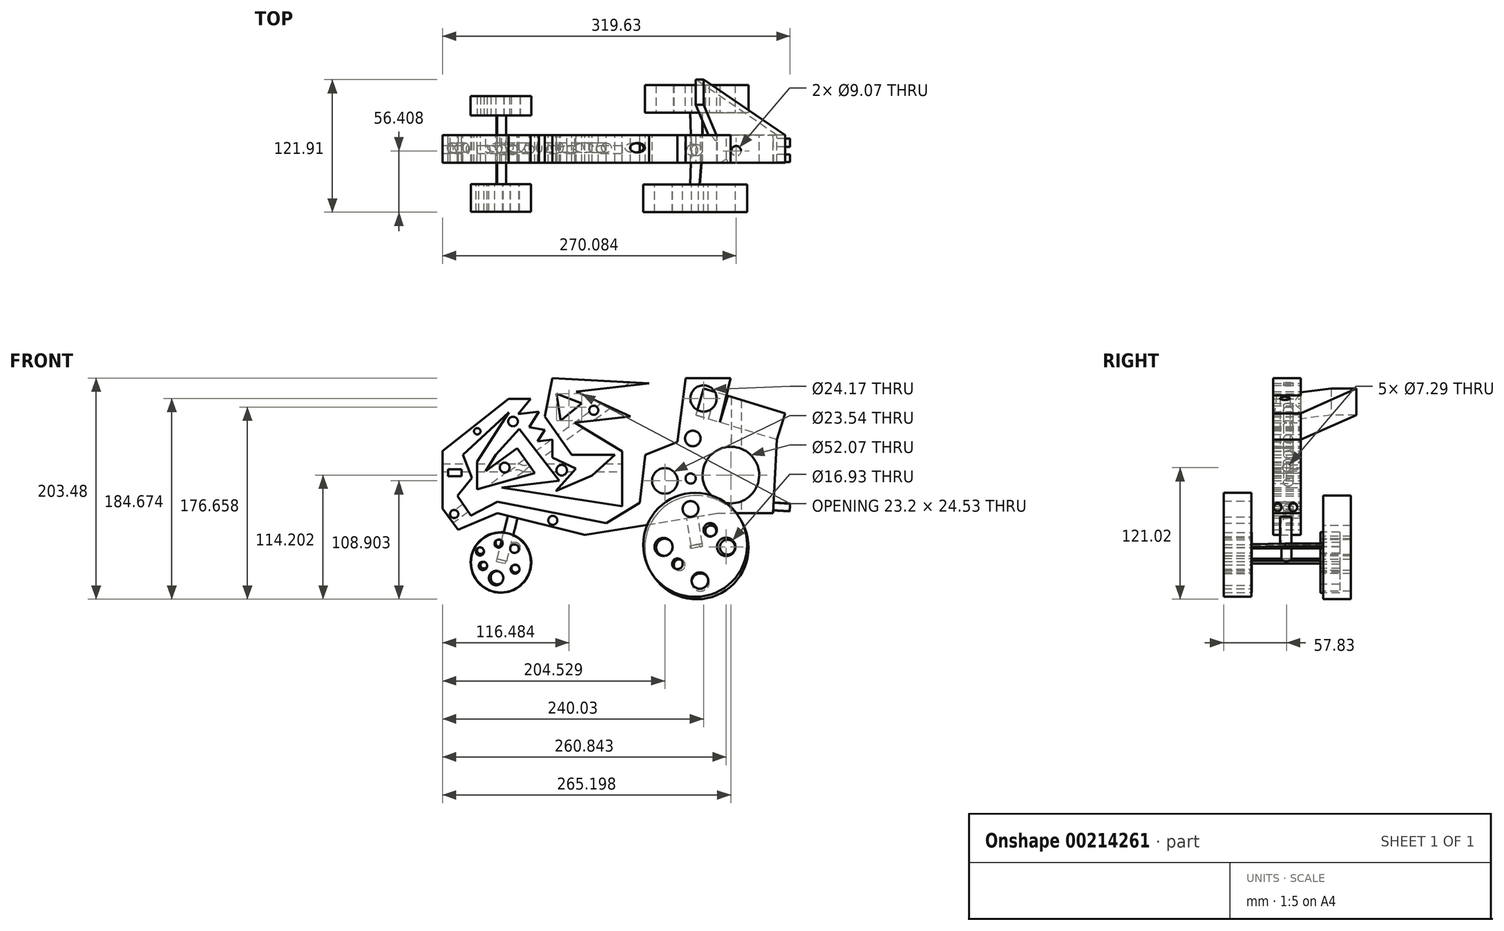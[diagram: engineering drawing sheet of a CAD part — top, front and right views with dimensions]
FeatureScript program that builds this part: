
annotation { "Feature Type Name" : "Feature", "Feature Type Description" : "" }
export const myFeature = defineFeature(function(context is Context, id is Id, definition is map)
    precondition{}
    {
        {
            var Q0;
            Q0=qCreatedBy(makeId("Front.planeOp"),FACE);
            var sketch = newSketch(context, id + "F0", { "sketchPlane" : qUnion([Q0])});
            skLineSegment(sketch, "E0", {"start": v(-109.42, 0) * mm, "end": v(-87.7, 23.84) * mm});
            skLineSegment(sketch, "E1", {"start": v(-87.7, 23.84) * mm, "end": v(-50.87, -23.58) * mm});
            skLineSegment(sketch, "E2", {"start": v(-50.87, -23.58) * mm, "end": v(-104.12, -29.94) * mm});
            skLineSegment(sketch, "E3", {"start": v(-104.12, -29.94) * mm, "end": v(6.89, -47.16) * mm});
            skLineSegment(sketch, "E4", {"start": v(6.89, -47.16) * mm, "end": v(6.89, 3.18) * mm});
            skLineSegment(sketch, "E5", {"start": v(6.89, 3.18) * mm, "end": v(-36.56, 29.67) * mm});
            skLineSegment(sketch, "E6", {"start": v(-36.56, 29.67) * mm, "end": v(14.3, 35.5) * mm});
            skLineSegment(sketch, "E7", {"start": v(14.3, 35.5) * mm, "end": v(-35.5, 58.28) * mm});
            skLineSegment(sketch, "E8", {"start": v(-35.5, 58.28) * mm, "end": v(31.53, 65.7) * mm});
            skLineSegment(sketch, "E9", {"start": v(31.53, 65.7) * mm, "end": v(-57.5, 70.73) * mm});
            skLineSegment(sketch, "E10", {"start": v(-57.5, 70.73) * mm, "end": v(-64.38, 35.5) * mm});
            skLineSegment(sketch, "E11", {"start": v(-64.38, 35.5) * mm, "end": v(-39.48, 0) * mm});
            skLineSegment(sketch, "E12", {"start": v(-39.48, 0) * mm, "end": v(0, 0) * mm});
            skLineSegment(sketch, "E13", {"start": v(0, 0) * mm, "end": v(-20.93, -19.08) * mm});
            skLineSegment(sketch, "E14", {"start": v(-20.93, -19.08) * mm, "end": v(-54.31, -33.12) * mm});
            skLineSegment(sketch, "E15", {"start": v(-54.31, -33.12) * mm, "end": v(-35.77, -12.45) * mm});
            skLineSegment(sketch, "E16", {"start": v(-35.77, -12.45) * mm, "end": v(-57.5, -2.52) * mm});
            skLineSegment(sketch, "E17", {"start": v(-57.5, -2.52) * mm, "end": v(-57.5, 14.04) * mm});
            skLineSegment(sketch, "E18", {"start": v(-57.5, 14.04) * mm, "end": v(-71.01, 12.54) * mm});
            skLineSegment(sketch, "E19", {"start": v(-71.01, 12.54) * mm, "end": v(-64.38, 23.05) * mm});
            skLineSegment(sketch, "E20", {"start": v(-64.38, 23.05) * mm, "end": v(-78.69, 25.43) * mm});
            skLineSegment(sketch, "E21", {"start": v(-78.69, 25.43) * mm, "end": v(-69.68, 39.74) * mm});
            skLineSegment(sketch, "E22", {"start": v(-69.68, 39.74) * mm, "end": v(-88.67, 37.64) * mm});
            skLineSegment(sketch, "E23", {"start": v(-88.67, 37.64) * mm, "end": v(-77.36, 51.4) * mm});
            skLineSegment(sketch, "E24", {"start": v(-77.36, 51.4) * mm, "end": v(-97.76, 51.4) * mm});
            skLineSegment(sketch, "E25", {"start": v(-97.76, 51.4) * mm, "end": v(-158.43, 3.44) * mm});
            skLineSegment(sketch, "E26", {"start": v(-158.43, 3.44) * mm, "end": v(-158.43, -49.28) * mm});
            skLineSegment(sketch, "E27", {"start": v(-158.43, -49.28) * mm, "end": v(-144.12, -68.89) * mm});
            skLineSegment(sketch, "E28", {"start": v(-144.12, -68.89) * mm, "end": v(-107.85, -53.63) * mm});
            skLineSegment(sketch, "E29", {"start": v(-107.85, -53.63) * mm, "end": v(-27.55, -73.65) * mm});
            skLineSegment(sketch, "E30", {"start": v(-27.55, -73.65) * mm, "end": v(94.32, -53.63) * mm});
            skLineSegment(sketch, "E31", {"start": v(94.32, -53.63) * mm, "end": v(145.45, -53.63) * mm});
            skLineSegment(sketch, "E32", {"start": v(145.45, -53.63) * mm, "end": v(149.16, 14.04) * mm});
            skLineSegment(sketch, "E33", {"start": v(149.16, 14.04) * mm, "end": v(96.7, 29.93) * mm});
            skLineSegment(sketch, "E34", {"start": v(96.7, 29.93) * mm, "end": v(106.5, 70.47) * mm});
            skLineSegment(sketch, "E35", {"start": v(106.5, 70.47) * mm, "end": v(65.17, 70.47) * mm});
            skLineSegment(sketch, "E36", {"start": v(65.17, 70.47) * mm, "end": v(57.5, 11.92) * mm});
            skLineSegment(sketch, "E37", {"start": v(57.5, 11.92) * mm, "end": v(28.08, 0) * mm});
            skLineSegment(sketch, "E38", {"start": v(28.08, 0) * mm, "end": v(23.05, -43.98) * mm});
            skLineSegment(sketch, "E39", {"start": v(23.05, -43.98) * mm, "end": v(-7.68, -62.8) * mm});
            skLineSegment(sketch, "E40", {"start": v(-7.68, -62.8) * mm, "end": v(-73.39, -49.81) * mm});
            skLineSegment(sketch, "E41", {"start": v(-73.39, -49.81) * mm, "end": v(-107.85, -43.19) * mm});
            skLineSegment(sketch, "E42", {"start": v(-107.85, -43.19) * mm, "end": v(-132.2, -55.64) * mm});
            skLineSegment(sketch, "E43", {"start": v(-132.2, -55.64) * mm, "end": v(-144.65, -37.62) * mm});
            skLineSegment(sketch, "E44", {"start": v(-144.65, -37.62) * mm, "end": v(-131.4, -21.2) * mm});
            skLineSegment(sketch, "E45", {"start": v(-131.4, -21.2) * mm, "end": v(-139.62, 0) * mm});
            skLineSegment(sketch, "E46", {"start": v(-139.62, 0) * mm, "end": v(-97.23, 39.2) * mm});
            skLineSegment(sketch, "E47", {"start": v(-97.23, 39.2) * mm, "end": v(-126.64, -6.1) * mm});
            skLineSegment(sketch, "E48", {"start": v(-126.64, -6.1) * mm, "end": v(-126.64, -31.53) * mm});
            skLineSegment(sketch, "E49", {"start": v(-126.64, -31.53) * mm, "end": v(-73.39, -16.7) * mm});
            skLineSegment(sketch, "E50", {"start": v(-73.39, -16.7) * mm, "end": v(-89.81, 6.1) * mm});
            skLineSegment(sketch, "E51", {"start": v(-89.81, 6.1) * mm, "end": v(-118.77, -14.79) * mm});
            skLineSegment(sketch, "E52", {"start": v(-118.77, -14.79) * mm, "end": v(-109.42, 0) * mm});
            skCircle(sketch, "E53", {"center": v(46.1, -23.85) * mm, "radius": 11.77 * mm});
            skCircle(sketch, "E54", {"center": v(81.6, 51.92) * mm, "radius": 12.08 * mm});
            skCircle(sketch, "E55", {"center": v(106.77, -18.55) * mm, "radius": 26.04 * mm});
            skCircle(sketch, "E56", {"center": v(-19.34, 41.06) * mm, "radius": 4.19 * mm});
            skCircle(sketch, "E57", {"center": v(-48.75, -14.04) * mm, "radius": 4.86 * mm});
            skLineSegment(sketch, "E58.bottom", {"start": v(-153.13, -19.6) * mm, "end": v(-140.68, -19.6) * mm});
            skLineSegment(sketch, "E58.top", {"start": v(-153.13, -13.25) * mm, "end": v(-140.68, -13.25) * mm});
            skLineSegment(sketch, "E58.left", {"start": v(-153.13, -19.6) * mm, "end": v(-153.13, -13.25) * mm});
            skLineSegment(sketch, "E58.right", {"start": v(-140.68, -19.6) * mm, "end": v(-140.68, -13.25) * mm});
            skCircle(sketch, "E59.cCircle", {"center": v(-44.5, 45.04) * mm, "radius": 7.17 * mm, "construction": true});
            skLineSegment(sketch, "E59.0", {"start": v(-53.54, 56.17) * mm, "end": v(-30.35, 47.3) * mm});
            skLineSegment(sketch, "E59.1", {"start": v(-30.35, 47.3) * mm, "end": v(-49.64, 31.64) * mm});
            skLineSegment(sketch, "E59.2", {"start": v(-49.64, 31.64) * mm, "end": v(-53.54, 56.17) * mm});
            skPoint(sketch, "E59.0.midPoint", {"position": v(-41.95, 51.73) * mm});
            skCircle(sketch, "E60", {"center": v(-101.2, -11.66) * mm, "radius": 4.5 * mm});
            skCircle(sketch, "E61", {"center": v(71.8, 15.1) * mm, "radius": 7.16 * mm});
            skCircle(sketch, "E62", {"center": v(-56.96, -60.14) * mm, "radius": 4.14 * mm});
            skCircle(sketch, "E63", {"center": v(-147.57, -54.31) * mm, "radius": 3.77 * mm});
            skCircle(sketch, "E64", {"center": v(-126.37, 21.72) * mm, "radius": 2.96 * mm});
            skCircle(sketch, "E65", {"center": v(-93.52, 30.73) * mm, "radius": 4.44 * mm});
            skSolve(sketch);
        }
        {
            var Q0;
            Q0 = qSketchRegion(id + "F0", true);
            extrude(context, id + "F1", {"entities" : qUnion([Q0]), "depth" : 25.4 * mm});
        }
        {
            var Q0;
            Q0=makeQuery(id+"F1.opExtrude","CAP_FACE",FACE,{"disambiguationData":[OSD([sQuery(id+"F0.wireOp",EDGE,"E0"),sQuery(id+"F0.wireOp",EDGE,"E1"),sQuery(id+"F0.wireOp",EDGE,"E2"),sQuery(id+"F0.wireOp",EDGE,"E3"),sQuery(id+"F0.wireOp",EDGE,"E4"),sQuery(id+"F0.wireOp",EDGE,"E5"),sQuery(id+"F0.wireOp",EDGE,"E6"),sQuery(id+"F0.wireOp",EDGE,"E7"),sQuery(id+"F0.wireOp",EDGE,"E8"),sQuery(id+"F0.wireOp",EDGE,"E9"),sQuery(id+"F0.wireOp",EDGE,"E10"),sQuery(id+"F0.wireOp",EDGE,"E11"),sQuery(id+"F0.wireOp",EDGE,"E12"),sQuery(id+"F0.wireOp",EDGE,"E13"),sQuery(id+"F0.wireOp",EDGE,"E14"),sQuery(id+"F0.wireOp",EDGE,"E15"),sQuery(id+"F0.wireOp",EDGE,"E16"),sQuery(id+"F0.wireOp",EDGE,"E17"),sQuery(id+"F0.wireOp",EDGE,"E18"),sQuery(id+"F0.wireOp",EDGE,"E19"),sQuery(id+"F0.wireOp",EDGE,"E20"),sQuery(id+"F0.wireOp",EDGE,"E21"),sQuery(id+"F0.wireOp",EDGE,"E22"),sQuery(id+"F0.wireOp",EDGE,"E23"),sQuery(id+"F0.wireOp",EDGE,"E24"),sQuery(id+"F0.wireOp",EDGE,"E25"),sQuery(id+"F0.wireOp",EDGE,"E26"),sQuery(id+"F0.wireOp",EDGE,"E27"),sQuery(id+"F0.wireOp",EDGE,"E28"),sQuery(id+"F0.wireOp",EDGE,"E29"),sQuery(id+"F0.wireOp",EDGE,"E30"),sQuery(id+"F0.wireOp",EDGE,"E31"),sQuery(id+"F0.wireOp",EDGE,"E32"),sQuery(id+"F0.wireOp",EDGE,"E33"),sQuery(id+"F0.wireOp",EDGE,"E34"),sQuery(id+"F0.wireOp",EDGE,"E35"),sQuery(id+"F0.wireOp",EDGE,"E36"),sQuery(id+"F0.wireOp",EDGE,"E37"),sQuery(id+"F0.wireOp",EDGE,"E38"),sQuery(id+"F0.wireOp",EDGE,"E39"),sQuery(id+"F0.wireOp",EDGE,"E40"),sQuery(id+"F0.wireOp",EDGE,"E41"),sQuery(id+"F0.wireOp",EDGE,"E42"),sQuery(id+"F0.wireOp",EDGE,"E43"),sQuery(id+"F0.wireOp",EDGE,"E44"),sQuery(id+"F0.wireOp",EDGE,"E45"),sQuery(id+"F0.wireOp",EDGE,"E46"),sQuery(id+"F0.wireOp",EDGE,"E47"),sQuery(id+"F0.wireOp",EDGE,"E48"),sQuery(id+"F0.wireOp",EDGE,"E49"),sQuery(id+"F0.wireOp",EDGE,"E50"),sQuery(id+"F0.wireOp",EDGE,"E51"),sQuery(id+"F0.wireOp",EDGE,"E52"),sQuery(id+"F0.wireOp",EDGE,"E53"),sQuery(id+"F0.wireOp",EDGE,"E54"),sQuery(id+"F0.wireOp",EDGE,"E55"),sQuery(id+"F0.wireOp",EDGE,"E56"),sQuery(id+"F0.wireOp",EDGE,"E57"),sQuery(id+"F0.wireOp",EDGE,"E58.bottom"),sQuery(id+"F0.wireOp",EDGE,"E58.top"),sQuery(id+"F0.wireOp",EDGE,"E58.left"),sQuery(id+"F0.wireOp",EDGE,"E58.right"),sQuery(id+"F0.wireOp",EDGE,"E59.0"),sQuery(id+"F0.wireOp",EDGE,"E59.1"),sQuery(id+"F0.wireOp",EDGE,"E59.2"),sQuery(id+"F0.wireOp",EDGE,"E60"),sQuery(id+"F0.wireOp",EDGE,"E61"),sQuery(id+"F0.wireOp",EDGE,"E62"),sQuery(id+"F0.wireOp",EDGE,"E63"),sQuery(id+"F0.wireOp",EDGE,"E64"),sQuery(id+"F0.wireOp",EDGE,"E65")])],"isStart":false});
            var sketch = newSketch(context, id + "F2", { "sketchPlane" : qUnion([Q0])});
            skCircle(sketch, "E66", {"center": v(69.81, -21.73) * mm, "radius": 4.69 * mm});
            skSolve(sketch);
        }
        {
            var Q0;
            Q0=makeQuery(id+"F1.opExtrude","SWEPT_FACE",FACE,{"disambiguationData":[OSD([sQuery(id+"F0.wireOp",EDGE,"E30")])]});
            var sketch = newSketch(context, id + "F3", { "sketchPlane" : qUnion([Q0])});
            skCircle(sketch, "E67", {"center": v(61, 13.82) * mm, "radius": 5.2 * mm});
            skSolve(sketch);
        }
        {
            var Q0;
            Q0 = qSketchRegion(id + "F3", true);
            extrude(context, id + "F4", {"entities" : qUnion([Q0]), "operationType" : NewBodyOperationType.ADD, "depth" : 25.4 * mm});
        }
        {
            var Q0;
            Q0=makeQuery(id+"F4.opExtrude","CAP_FACE",FACE,{"disambiguationData":[OSD([sQuery(id+"F3.wireOp",EDGE,"E67")])],"isStart":false});
            var sketch = newSketch(context, id + "F5", { "sketchPlane" : qUnion([Q0])});
            skLineSegment(sketch, "E68", {"start": v(55.8, 13.66) * mm, "end": v(54.82, 45.47) * mm});
            skLineSegment(sketch, "E69", {"start": v(54.82, 45.47) * mm, "end": v(63.54, 45.47) * mm});
            skLineSegment(sketch, "E70", {"start": v(63.54, 45.47) * mm, "end": v(66.18, 14.26) * mm});
            skLineSegment(sketch, "E71", {"start": v(66.18, 14.26) * mm, "end": v(66.18, -20.71) * mm});
            skLineSegment(sketch, "E72", {"start": v(66.18, -20.71) * mm, "end": v(54.82, -20.71) * mm});
            skLineSegment(sketch, "E73", {"start": v(54.82, -20.71) * mm, "end": v(55.8, 13.66) * mm});
            skSolve(sketch);
        }
        {
            var Q0;
            Q0 = qSketchRegion(id + "F5", true);
            extrude(context, id + "F6", {"entities" : qUnion([Q0]), "operationType" : NewBodyOperationType.ADD, "depth" : 2.54 * mm});
        }
        {
            var Q0;
            Q0=makeQuery(id+"F6.opExtrude","SWEPT_FACE",FACE,{"disambiguationData":[OSD([sQuery(id+"F5.wireOp",EDGE,"E69")])]});
            var sketch = newSketch(context, id + "F7", { "sketchPlane" : qUnion([Q0])});
            skCircle(sketch, "E74", {"center": v(74, -82.7) * mm, "radius": 47.8 * mm});
            skPoint(sketch, "E74.centerSnap0", {"position": v(74, -85.28) * mm});
            skCircle(sketch, "E75", {"center": v(44.83, -84.58) * mm, "radius": 8.29 * mm});
            skCircle(sketch, "E76", {"center": v(102.41, -84.58) * mm, "radius": 8.47 * mm});
            skCircle(sketch, "E77", {"center": v(69.67, -49.72) * mm, "radius": 7.23 * mm});
            skCircle(sketch, "E78", {"center": v(78.3, -115.58) * mm, "radius": 7.57 * mm});
            skCircle(sketch, "E79", {"center": v(87.73, -68.91) * mm, "radius": 6.13 * mm});
            skCircle(sketch, "E80", {"center": v(57.63, -100.15) * mm, "radius": 4.9 * mm});
            skSolve(sketch);
        }
        {
            var Q0;
            Q0 = qSketchRegion(id + "F7", true);
            extrude(context, id + "F8", {"entities" : qUnion([Q0]), "operationType" : NewBodyOperationType.ADD, "depth" : 25.4 * mm});
        }
        {
            var Q0;
            Q0=makeQuery(id+"F6.opExtrude","SWEPT_FACE",FACE,{"disambiguationData":[OSD([sQuery(id+"F5.wireOp",EDGE,"E72")])]});
            var sketch = newSketch(context, id + "F9", { "sketchPlane" : qUnion([Q0])});
            skCircle(sketch, "E81", {"center": v(-75.3, -85.07) * mm, "radius": 47.68 * mm});
            skCircle(sketch, "E82", {"center": v(-88.33, -69.95) * mm, "radius": 5 * mm});
            skCircle(sketch, "E83", {"center": v(-103.62, -84.84) * mm, "radius": 6.9 * mm});
            skCircle(sketch, "E84", {"center": v(-78.72, -117.13) * mm, "radius": 8.17 * mm});
            skCircle(sketch, "E85", {"center": v(-59.49, -101.18) * mm, "radius": 5.2 * mm});
            skCircle(sketch, "E86", {"center": v(-45.9, -85) * mm, "radius": 7.87 * mm});
            skSolve(sketch);
        }
        {
            var Q0;
            Q0 = qSketchRegion(id + "F9", true);
            extrude(context, id + "F10", {"entities" : qUnion([Q0]), "operationType" : NewBodyOperationType.ADD, "depth" : 25.4 * mm});
        }
        {
            var Q0;
            Q0=makeQuery(id+"F1.opExtrude","SWEPT_FACE",FACE,{"disambiguationData":[OSD([sQuery(id+"F0.wireOp",EDGE,"E29")])]});
            var sketch = newSketch(context, id + "F11", { "sketchPlane" : qUnion([Q0])});
            skCircle(sketch, "E87", {"center": v(-77.25, 13.22) * mm, "radius": 4.58 * mm});
            skSolve(sketch);
        }
        {
            var Q0;
            Q0 = qSketchRegion(id + "F11", true);
            extrude(context, id + "F12", {"entities" : qUnion([Q0]), "operationType" : NewBodyOperationType.ADD, "depth" : 40.64 * mm});
        }
        {
            var Q0;
            Q0=makeQuery(id+"F12.opExtrude","CAP_FACE",FACE,{"disambiguationData":[OSD([sQuery(id+"F11.wireOp",EDGE,"E87")])],"isStart":false});
            var sketch = newSketch(context, id + "F13", { "sketchPlane" : qUnion([Q0])});
            skLineSegment(sketch, "E88", {"start": v(-81.83, 13.22) * mm, "end": v(-81.83, 45.01) * mm});
            skLineSegment(sketch, "E89", {"start": v(-81.83, 13.22) * mm, "end": v(-81.83, -18.02) * mm});
            skLineSegment(sketch, "E90", {"start": v(-81.83, -18.02) * mm, "end": v(-73.29, -18.02) * mm});
            skLineSegment(sketch, "E91", {"start": v(-73.29, -18.02) * mm, "end": v(-73.29, 45.01) * mm});
            skLineSegment(sketch, "E92", {"start": v(-73.29, 45.01) * mm, "end": v(-81.83, 45.01) * mm});
            skSolve(sketch);
        }
        {
            var Q0;
            Q0 = qSketchRegion(id + "F13", true);
            extrude(context, id + "F14", {"entities" : qUnion([Q0]), "operationType" : NewBodyOperationType.ADD, "depth" : 2.54 * mm});
        }
        {
            var Q0;
            Q0=makeQuery(id+"F14.opExtrude","SWEPT_FACE",FACE,{"disambiguationData":[OSD([sQuery(id+"F13.wireOp",EDGE,"E92")])]});
            var sketch = newSketch(context, id + "F15", { "sketchPlane" : qUnion([Q0])});
            skCircle(sketch, "E93", {"center": v(-104.61, -98.94) * mm, "radius": 27.53 * mm});
            skCircle(sketch, "E94", {"center": v(-123.92, -88.83) * mm, "radius": 3.7 * mm});
            skCircle(sketch, "E95", {"center": v(-121.2, -102.04) * mm, "radius": 3.89 * mm});
            skCircle(sketch, "E96", {"center": v(-109.07, -113.28) * mm, "radius": 6.6 * mm});
            skCircle(sketch, "E97", {"center": v(-91.68, -105.14) * mm, "radius": 4.05 * mm});
            skCircle(sketch, "E98", {"center": v(-92.17, -86.24) * mm, "radius": 3.95 * mm});
            skCircle(sketch, "E99", {"center": v(-106.82, -81.58) * mm, "radius": 3.68 * mm});
            skSolve(sketch);
        }
        {
            var Q0;
            Q0 = qSketchRegion(id + "F15", true);
            extrude(context, id + "F16", {"entities" : qUnion([Q0]), "operationType" : NewBodyOperationType.ADD, "depth" : 17.78 * mm});
        }
        {
            var Q0;
            Q0 = qSketchRegion(id + "F15", true);
            extrude(context, id + "F17", {"entities" : qUnion([Q0]), "operationType" : NewBodyOperationType.ADD, "depth" : 25.4 * mm});
        }
        {
            var Q0;
            Q0=makeQuery(id+"F14.opExtrude","SWEPT_FACE",FACE,{"disambiguationData":[OSD([sQuery(id+"F13.wireOp",EDGE,"E90")])]});
            var sketch = newSketch(context, id + "F18", { "sketchPlane" : qUnion([Q0])});
            skCircle(sketch, "E100", {"center": v(104.61, -98.94) * mm, "radius": 27.83 * mm});
            skCircle(sketch, "E101", {"center": v(91.72, -85.35) * mm, "radius": 4.94 * mm});
            skCircle(sketch, "E102", {"center": v(105.86, -80.86) * mm, "radius": 3.6 * mm});
            skCircle(sketch, "E103", {"center": v(123.4, -87.94) * mm, "radius": 3.12 * mm});
            skCircle(sketch, "E104", {"center": v(120.36, -101.49) * mm, "radius": 3.02 * mm});
            skCircle(sketch, "E105", {"center": v(107.94, -112.93) * mm, "radius": 6.07 * mm});
            skCircle(sketch, "E106", {"center": v(91.15, -104.27) * mm, "radius": 3.82 * mm});
            skSolve(sketch);
        }
        {
            var Q0;
            Q0 = qSketchRegion(id + "F18", true);
            extrude(context, id + "F19", {"entities" : qUnion([Q0]), "operationType" : NewBodyOperationType.ADD, "depth" : 17.78 * mm});
        }
        {
            var Q0;
            Q0 = qSketchRegion(id + "F2", true);
            extrude(context, id + "F20", {"entities" : qUnion([Q0]), "operationType" : NewBodyOperationType.REMOVE, "endBound" : BoundingType.THROUGH_ALL, "oppositeDirection" : true, "depth" : 25.4 * mm});
        }
        {
            var Q0;
            Q0=makeQuery(id+"F1.opExtrude","SWEPT_FACE",FACE,{"disambiguationData":[OSD([sQuery(id+"F0.wireOp",EDGE,"E4")])]});
            var sketch = newSketch(context, id + "F21", { "sketchPlane" : qUnion([Q0])});
            skCircle(sketch, "E107", {"center": v(-13.04, -11.73) * mm, "radius": 3.65 * mm});
            skSolve(sketch);
        }
        {
            var Q0;
            Q0 = qSketchRegion(id + "F21", true);
            extrude(context, id + "F22", {"entities" : qUnion([Q0]), "operationType" : NewBodyOperationType.REMOVE, "endBound" : BoundingType.THROUGH_ALL, "oppositeDirection" : true, "depth" : 25.4 * mm});
        }
        {
            var Q0;
            Q0=makeQuery(id+"F1.opExtrude","SWEPT_FACE",FACE,{"disambiguationData":[OSD([sQuery(id+"F0.wireOp",EDGE,"E32")])]});
            var sketch = newSketch(context, id + "F23", { "sketchPlane" : qUnion([Q0])});
            skCircle(sketch, "E108", {"center": v(-21.24, -39.46) * mm, "radius": 3.48 * mm});
            skCircle(sketch, "E109", {"center": v(-6.96, -39.46) * mm, "radius": 3.67 * mm});
            skSolve(sketch);
        }
        {
            var Q0;
            Q0 = qSketchRegion(id + "F23", true);
            extrude(context, id + "F24", {"entities" : qUnion([Q0]), "operationType" : NewBodyOperationType.ADD, "depth" : 15.24 * mm});
        }
        {
            var Q0;
            Q0=makeQuery(id+"F1.opExtrude","SWEPT_FACE",FACE,{"disambiguationData":[OSD([sQuery(id+"F0.wireOp",EDGE,"E33")])]});
            var sketch = newSketch(context, id + "F25", { "sketchPlane" : qUnion([Q0])});
            skLineSegment(sketch, "E110", {"start": v(60.65, 28.09) * mm, "end": v(138.68, -25.4) * mm});
            skLineSegment(sketch, "E111", {"start": v(138.68, -25.4) * mm, "end": v(138.68, 0) * mm});
            skLineSegment(sketch, "E112", {"start": v(138.68, 0) * mm, "end": v(60.65, 51.04) * mm});
            skLineSegment(sketch, "E113", {"start": v(60.65, 51.04) * mm, "end": v(60.65, 28.09) * mm});
            skLineSegment(sketch, "E114", {"start": v(60.65, 28.09) * mm, "end": v(83.86, -25.4) * mm});
            skLineSegment(sketch, "E115", {"start": v(83.86, -25.4) * mm, "end": v(138.68, -25.4) * mm});
            skLineSegment(sketch, "E116", {"start": v(138.68, 0) * mm, "end": v(89.45, 0) * mm});
            skLineSegment(sketch, "E117", {"start": v(89.45, 0) * mm, "end": v(83.86, 0) * mm});
            skSolve(sketch);
        }
        {
            var Q0;
            Q0 = qSketchRegion(id + "F25", true);
            extrude(context, id + "F26", {"entities" : qUnion([Q0]), "operationType" : NewBodyOperationType.ADD, "depth" : 25.4 * mm});
        }
        {
            var Q0;
            Q0=makeQuery(id+"F1.opExtrude","SWEPT_FACE",FACE,{"disambiguationData":[OSD([sQuery(id+"F0.wireOp",EDGE,"E31")])]});
            var sketch = newSketch(context, id + "F27", { "sketchPlane" : qUnion([Q0])});
            skCircle(sketch, "E118", {"center": v(111.65, 14.46) * mm, "radius": 4.54 * mm});
            skSolve(sketch);
        }
        {
            var Q0;
            Q0 = qSketchRegion(id + "F27", true);
            extrude(context, id + "F28", {"entities" : qUnion([Q0]), "operationType" : NewBodyOperationType.REMOVE, "endBound" : BoundingType.THROUGH_ALL, "oppositeDirection" : true, "depth" : 25.4 * mm});
        }
        {
            var Q0;
            Q0=makeQuery(id+"F1.opExtrude","SWEPT_FACE",FACE,{"disambiguationData":[OSD([sQuery(id+"F0.wireOp",EDGE,"E27")])]});
            var sketch = newSketch(context, id + "F29", { "sketchPlane" : qUnion([Q0])});
            skCircle(sketch, "E119", {"center": v(11.65, 41.28) * mm, "radius": 4.34 * mm});
            skSolve(sketch);
        }
        {
            var Q0;
            Q0 = qSketchRegion(id + "F29", true);
            extrude(context, id + "F30", {"entities" : qUnion([Q0]), "operationType" : NewBodyOperationType.REMOVE, "endBound" : BoundingType.THROUGH_ALL, "oppositeDirection" : true, "depth" : 25.4 * mm});
        }
    });
